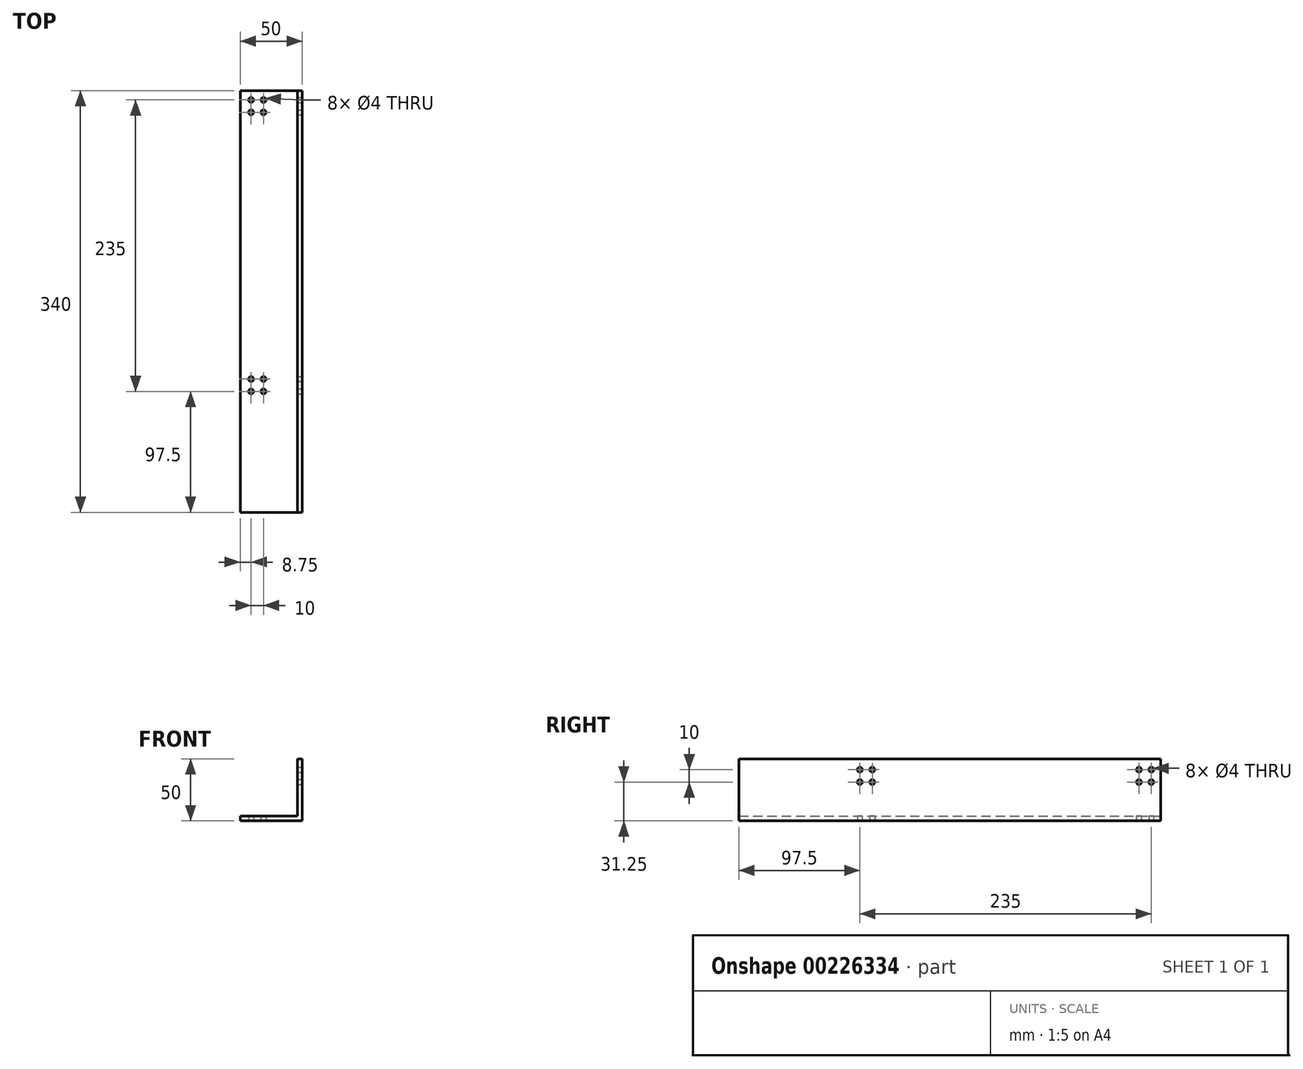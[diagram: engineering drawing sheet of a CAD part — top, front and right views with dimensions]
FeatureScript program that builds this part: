
annotation { "Feature Type Name" : "Feature", "Feature Type Description" : "" }
export const myFeature = defineFeature(function(context is Context, id is Id, definition is map)
    precondition{}
    {
        {
            var Q0;
            Q0=qCreatedBy(makeId("Front.planeOp"),FACE);
            var sketch = newSketch(context, id + "F0", { "sketchPlane" : qUnion([Q0])});
            skLineSegment(sketch, "E0.bottom", {"start": v(0, 0) * mm, "end": v(4, 0) * mm});
            skLineSegment(sketch, "E0.top", {"start": v(0, 46) * mm, "end": v(4, 46) * mm});
            skLineSegment(sketch, "E0.left", {"start": v(0, 0) * mm, "end": v(0, 46) * mm});
            skLineSegment(sketch, "E0.right", {"start": v(4, 0) * mm, "end": v(4, 46) * mm});
            skLineSegment(sketch, "E1.bottom", {"start": v(4, 0) * mm, "end": v(-46, 0) * mm});
            skLineSegment(sketch, "E1.top", {"start": v(4, -4) * mm, "end": v(-46, -4) * mm});
            skLineSegment(sketch, "E1.left", {"start": v(4, 0) * mm, "end": v(4, -4) * mm});
            skLineSegment(sketch, "E1.right", {"start": v(-46, 0) * mm, "end": v(-46, -4) * mm});
            skSolve(sketch);
        }
        {
            var Q0;
            Q0 = qSketchRegion(id + "F0", true);
            extrude(context, id + "F1", {"entities" : qUnion([Q0]), "depth" : 125 * mm});
        }
        {
            var Q0;
            Q0=makeQuery(id+"F1.opExtrude","SWEPT_FACE",FACE,{"disambiguationData":[OSD([sQuery(id+"F0.wireOp",EDGE,"E1.top")])]});
            var sketch = newSketch(context, id + "F2", { "sketchPlane" : qUnion([Q0])});
            skLineSegment(sketch, "E2.bottom", {"start": v(-46, 125) * mm, "end": v(-21, 125) * mm});
            skLineSegment(sketch, "E2.top", {"start": v(-46, 100) * mm, "end": v(-21, 100) * mm});
            skLineSegment(sketch, "E2.left", {"start": v(-46, 125) * mm, "end": v(-46, 100) * mm});
            skLineSegment(sketch, "E2.right", {"start": v(-21, 125) * mm, "end": v(-21, 100) * mm});
            skLineSegment(sketch, "E3", {"start": v(-46, 125) * mm, "end": v(-46, 122.5) * mm});
            skLineSegment(sketch, "E4.bottom", {"start": v(-46, 122.5) * mm, "end": v(-21, 122.5) * mm});
            skLineSegment(sketch, "E4.top", {"start": v(-46, 102.5) * mm, "end": v(-21, 102.5) * mm});
            skLineSegment(sketch, "E4.left", {"start": v(-46, 122.5) * mm, "end": v(-46, 102.5) * mm});
            skLineSegment(sketch, "E4.right", {"start": v(-21, 122.5) * mm, "end": v(-21, 102.5) * mm});
            skLineSegment(sketch, "E5", {"start": v(-46, 122.5) * mm, "end": v(-46, 112.5) * mm});
            skLineSegment(sketch, "E6", {"start": v(-46, 112.5) * mm, "end": v(-46, 102.5) * mm});
            skLineSegment(sketch, "E7", {"start": v(-46, 107.5) * mm, "end": v(-25.75, 107.5) * mm});
            skLineSegment(sketch, "E8", {"start": v(-25.75, 107.5) * mm, "end": v(-28.5, 107.5) * mm});
            skLineSegment(sketch, "E9", {"start": v(-28.5, 107.5) * mm, "end": v(-46, 107.5) * mm});
            skLineSegment(sketch, "E10", {"start": v(-46, 117.5) * mm, "end": v(-25.75, 117.5) * mm});
            skLineSegment(sketch, "E11", {"start": v(-25.75, 117.5) * mm, "end": v(-28.5, 117.5) * mm});
            skLineSegment(sketch, "E12", {"start": v(-28.5, 117.5) * mm, "end": v(-46, 117.5) * mm});
            skCircle(sketch, "E13", {"center": v(-37.25, 117.5) * mm, "radius": 1.5 * mm});
            skCircle(sketch, "E14", {"center": v(-27.25, 117.5) * mm, "radius": 1.5 * mm});
            skCircle(sketch, "E15", {"center": v(-27.25, 107.5) * mm, "radius": 1.5 * mm});
            skCircle(sketch, "E16", {"center": v(-37.25, 107.5) * mm, "radius": 1.5 * mm});
            skSolve(sketch);
        }
        {
            var Q0;
            Q0=makeQuery(id+"F1.opExtrude","SWEPT_FACE",FACE,{"disambiguationData":[OSD([sQuery(id+"F0.wireOp",EDGE,"E0.right"),sQuery(id+"F0.wireOp",EDGE,"E1.left")])]});
            var sketch = newSketch(context, id + "F3", { "sketchPlane" : qUnion([Q0])});
            skLineSegment(sketch, "E17.bottom", {"start": v(-125, 46) * mm, "end": v(-100, 46) * mm});
            skLineSegment(sketch, "E17.top", {"start": v(-125, 21) * mm, "end": v(-100, 21) * mm});
            skLineSegment(sketch, "E17.left", {"start": v(-125, 46) * mm, "end": v(-125, 21) * mm});
            skLineSegment(sketch, "E17.right", {"start": v(-100, 46) * mm, "end": v(-100, 21) * mm});
            skLineSegment(sketch, "E18", {"start": v(-125, 46) * mm, "end": v(-122.5, 46) * mm});
            skLineSegment(sketch, "E19.bottom", {"start": v(-122.5, 46) * mm, "end": v(-102.5, 46) * mm});
            skLineSegment(sketch, "E19.top", {"start": v(-122.5, 21) * mm, "end": v(-102.5, 21) * mm});
            skLineSegment(sketch, "E19.left", {"start": v(-122.5, 46) * mm, "end": v(-122.5, 21) * mm});
            skLineSegment(sketch, "E19.right", {"start": v(-102.5, 46) * mm, "end": v(-102.5, 21) * mm});
            skLineSegment(sketch, "E20", {"start": v(-122.5, 46) * mm, "end": v(-112.5, 46) * mm});
            skLineSegment(sketch, "E21", {"start": v(-112.5, 46) * mm, "end": v(-102.5, 46) * mm});
            skLineSegment(sketch, "E22", {"start": v(-107.5, 46) * mm, "end": v(-107.5, 25.75) * mm});
            skLineSegment(sketch, "E23", {"start": v(-107.5, 25.75) * mm, "end": v(-107.5, 28.5) * mm});
            skLineSegment(sketch, "E24", {"start": v(-107.5, 28.5) * mm, "end": v(-107.5, 46) * mm});
            skLineSegment(sketch, "E25", {"start": v(-117.5, 46) * mm, "end": v(-117.5, 25.75) * mm});
            skLineSegment(sketch, "E26", {"start": v(-117.5, 25.75) * mm, "end": v(-117.5, 28.5) * mm});
            skLineSegment(sketch, "E27", {"start": v(-117.5, 28.5) * mm, "end": v(-117.5, 46) * mm});
            skCircle(sketch, "E28", {"center": v(-117.5, 37.25) * mm, "radius": 1.5 * mm});
            skCircle(sketch, "E29", {"center": v(-117.5, 27.25) * mm, "radius": 1.5 * mm});
            skCircle(sketch, "E30", {"center": v(-107.5, 27.25) * mm, "radius": 1.5 * mm});
            skCircle(sketch, "E31", {"center": v(-107.5, 37.25) * mm, "radius": 1.5 * mm});
            skSolve(sketch);
        }
        {
            var Q0;
            Q0=sQuery(id+"F3.wireOp",VERTEX,"E28.center");
            var Q1;
            Q1=sQuery(id+"F3.wireOp",VERTEX,"E31.center");
            var Q2;
            Q2=sQuery(id+"F3.wireOp",VERTEX,"E30.center");
            var Q3;
            Q3=sQuery(id+"F3.wireOp",VERTEX,"E29.center");
            var Q4;
            Q4=sQuery(id+"F2.wireOp",VERTEX,"E14.center");
            var Q5;
            Q5=sQuery(id+"F2.wireOp",VERTEX,"E13.center");
            var Q6;
            Q6=sQuery(id+"F2.wireOp",VERTEX,"E16.center");
            var Q7;
            Q7=sQuery(id+"F2.wireOp",VERTEX,"E15.center");
            var Q8;
            Q8=makeQuery(id+"F1.opExtrude","SWEPT_BODY",BODY,{"disambiguationData":[OSD([sQuery(id+"F0.wireOp",EDGE,"E0.top"),sQuery(id+"F0.wireOp",EDGE,"E0.left"),sQuery(id+"F0.wireOp",EDGE,"E0.right"),sQuery(id+"F0.wireOp",EDGE,"E1.bottom"),sQuery(id+"F0.wireOp",EDGE,"E1.top"),sQuery(id+"F0.wireOp",EDGE,"E1.left"),sQuery(id+"F0.wireOp",EDGE,"E1.right")])]});
            hole(context, id + "F4", {"style" : HoleStyle.SIMPLE, "endStyle" : HoleEndStyle.BLIND, "holeDiameter" : 4 * mm, "holeDepth" : 15 * mm, "locations" : qUnion([Q0, Q1, Q2, Q3, Q4, Q5, Q6, Q7]), "scope" : qUnion([Q8])});
        }
        {
            var Q0;
            Q0=makeQuery(id+"F1.opExtrude","SWEPT_BODY",BODY,{"disambiguationData":[OSD([sQuery(id+"F0.wireOp",EDGE,"E0.top"),sQuery(id+"F0.wireOp",EDGE,"E0.left"),sQuery(id+"F0.wireOp",EDGE,"E0.right"),sQuery(id+"F0.wireOp",EDGE,"E1.bottom"),sQuery(id+"F0.wireOp",EDGE,"E1.top"),sQuery(id+"F0.wireOp",EDGE,"E1.left"),sQuery(id+"F0.wireOp",EDGE,"E1.right")])]});
            var Q1;
            Q1=makeQuery(id+"F1.opExtrude","CAP_FACE",FACE,{"disambiguationData":[OSD([sQuery(id+"F0.wireOp",EDGE,"E0.top"),sQuery(id+"F0.wireOp",EDGE,"E0.left"),sQuery(id+"F0.wireOp",EDGE,"E0.right"),sQuery(id+"F0.wireOp",EDGE,"E1.bottom"),sQuery(id+"F0.wireOp",EDGE,"E1.top"),sQuery(id+"F0.wireOp",EDGE,"E1.left"),sQuery(id+"F0.wireOp",EDGE,"E1.right")])],"isStart":true});
            mirror(context, id + "F5", {"operationType" : NewBodyOperationType.ADD, "entities" : qUnion([Q0]), "mirrorPlane" : qUnion([Q1])});
        }
        {
            var Q0;
            Q0=makeQuery(id+"F1.opExtrude","CAP_FACE",FACE,{"disambiguationData":[OSD([sQuery(id+"F0.wireOp",EDGE,"E0.top"),sQuery(id+"F0.wireOp",EDGE,"E0.left"),sQuery(id+"F0.wireOp",EDGE,"E0.right"),sQuery(id+"F0.wireOp",EDGE,"E1.bottom"),sQuery(id+"F0.wireOp",EDGE,"E1.top"),sQuery(id+"F0.wireOp",EDGE,"E1.left"),sQuery(id+"F0.wireOp",EDGE,"E1.right")])],"isStart":false});
            extrude(context, id + "F6", {"entities" : qUnion([Q0]), "operationType" : NewBodyOperationType.ADD, "depth" : 90 * mm});
        }
    });
